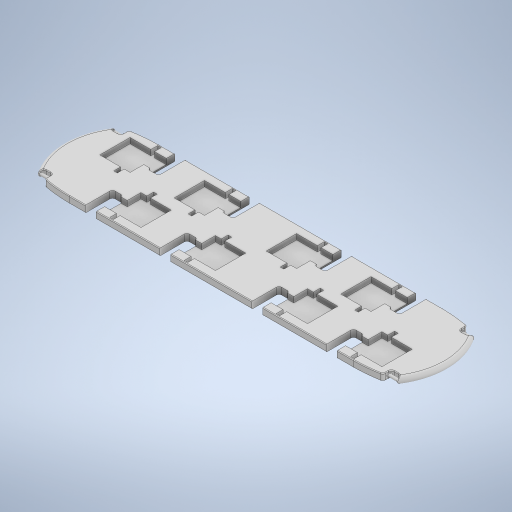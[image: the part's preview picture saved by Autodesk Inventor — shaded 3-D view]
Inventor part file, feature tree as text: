
AUTODESK INVENTOR PART (.ipt)
format: ipt  version: 2023.1 (Build 271208000, 208)  size: 1,013,760 bytes
history: native  units: mm
features: extrude x22, sketch x13, fillet x6
ambient origin geometry x8: Origin, YZ Plane, XZ Plane, XY Plane, X Axis, Y Axis, Z Axis, Center Point
bodies: Solid1 (feature_tree)
feature tree (41):
  sketch  "Sketch1"  dims[d0=250.0mm d1=66.0mm]
  extrude  "Extrusion1"  Depth=66.0mm
  sketch  "Sketch2"  dims[d3=34.0mm d4=55.0mm]
  extrude  "Extrusion2"  Depth=55.0mm
  extrude  "Extrusion3"  Depth=55.0mm
  extrude  "Extrusion20"  Depth=34.0mm
  fillet  "Fillet1"  Radius=55.0mm
  fillet  "Fillet2"  Radius=34.0mm
  fillet  "Fillet3"  Radius=55.0mm
  fillet  "Fillet4"  Radius=8.0mm
  extrude  "Extrusion21"  Depth=26.85mm
  extrude  "Extrusion22"  Depth=8.85mm
  extrude  "Extrusion23"  Depth=5.05mm
  extrude  "Extrusion24"  Depth=12.25mm
  fillet  "Fillet5"  Radius=2.65mm
  fillet  "Fillet6"  Radius=4.35mm
  sketch  "Sketch12"  dims[d26=5.0mm d27=0.0mm d28=4.0mm d29=0.0mm]
  sketch  "Sketch13"  dims[d53=2.65mm d54=4.35mm d55=4.35mm d56=2.65mm d57=12.25mm d58=4.45mm d59=5.05mm d60=5.05mm d61=8.85mm d62=26.85mm d63=32.45mm d64=8.0mm d65=20.0mm d66=55.0mm d67=34.0mm d68=55.0mm d69=34.0mm d71=0.0mm d72=5.0mm d74=0.0mm d75=4.0mm]
  sketch  "Sketch14"  dims[d76=1.15mm]
  sketch  "Sketch15"  dims[d78=2.65mm d79=4.35mm d80=4.35mm d81=2.65mm d82=12.25mm d83=4.45mm d84=5.05mm d85=5.05mm d86=8.85mm d87=26.85mm d88=32.45mm d89=8.0mm d90=20.0mm d91=55.0mm d92=34.0mm d93=55.0mm d94=34.0mm d96=0.0mm d97=5.0mm d99=0.0mm d100=4.0mm d101=1.15mm d103=2.65mm d104=4.35mm d105=4.35mm d106=2.65mm d107=12.25mm d108=4.45mm d109=5.05mm d110=5.05mm d111=8.85mm d112=26.85mm d113=32.45mm d114=8.0mm d115=20.0mm d116=55.0mm d117=34.0mm d118=55.0mm d119=34.0mm d121=0.0mm d122=5.0mm d124=0.0mm d125=4.0mm d126=1.15mm d127=2.65mm d128=4.35mm d129=4.35mm d130=2.65mm d131=12.25mm d133=5.05mm d135=8.85mm d136=26.85mm d137=32.45mm d138=8.0mm d139=20.0mm d140=55.0mm d141=34.0mm d142=55.0mm d145=0.0mm d146=5.0mm d148=0.0mm d149=4.0mm d150=1.15mm d151=22.35mm d152=5.05mm d154=4.45mm d156=2.65mm d157=4.35mm d158=4.35mm d159=2.65mm d160=5.05mm d161=4.45mm d162=22.35mm d163=12.25mm d164=5.05mm d165=8.85mm d166=26.85mm d167=32.45mm d168=8.0mm d169=20.0mm d170=55.0mm d171=34.0mm d172=55.0mm d174=0.0mm d175=5.0mm d177=0.0mm d178=4.0mm d180=1.15mm d182=2.65mm d183=4.35mm d184=4.35mm d185=2.65mm d186=5.05mm d187=4.45mm d188=22.35mm d189=12.25mm d190=5.05mm d191=8.85mm d192=26.85mm d193=32.45mm d194=8.0mm d195=20.0mm d196=55.0mm d197=34.0mm d198=55.0mm d200=0.0mm d201=5.0mm d203=0.0mm d204=4.0mm d205=34.0mm d207=2.65mm d208=4.35mm d209=4.35mm d210=2.65mm d211=5.05mm d212=4.45mm d213=22.35mm d214=12.25mm d215=5.05mm d216=8.85mm d217=26.85mm d218=32.45mm d219=8.0mm d220=20.0mm d221=55.0mm d222=34.0mm d223=55.0mm d224=34.0mm d226=0.0mm d227=5.0mm d229=0.0mm d230=4.0mm d231=7.0mm d232=7.0mm d233=50.0mm d234=50.0mm d235=13.0mm d236=66.0mm d237=13.0mm d238=66.0mm d239=20.0mm d240=25.0mm d241=40.0mm d242=5.0mm d243=0.0mm d244=50.0mm d245=2.5mm d246=2.0mm d247=0.5mm d248=2.0mm d249=7.5mm d250=0.0mm d251=7.5mm d252=0.0mm d253=2.0mm d254=7.5mm d255=0.0mm d256=2.0mm d257=7.5mm d258=0.0mm d259=0.4mm d260=0.4mm]
  sketch  "Sketch4"  dims[d5=34.0mm d6=55.0mm]
  sketch  "Sketch5"  dims[d7=5.0mm d8=0.0mm d9=34.0mm d10=55.0mm d11=34.0mm d12=55.0mm d13=8.0mm]
  sketch  "Sketch6"  dims[d14=20.0mm d15=26.85mm]
  sketch  "Sketch7"  dims[d16=32.45mm d17=8.85mm]
  sketch  "Sketch8"  dims[d18=5.05mm d19=5.05mm]
  sketch  "Sketch9"  dims[d20=4.45mm d21=12.25mm d22=2.65mm d23=4.35mm]
  sketch  "Sketch10"  dims[d24=4.35mm d25=2.65mm]
  extrude  "Extrusion6"  Depth=2.65mm
  extrude  "Extrusion7"  Depth=4.0mm TaperAngle=0.0deg
  extrude  "Extrusion8"  Depth=4.0mm TaperAngle=0.0deg
  extrude  "Extrusion9"  Depth=4.0mm TaperAngle=0.0deg
  extrude  "Extrusion10"  Depth=1.15mm
  extrude  "Extrusion11"  Depth=4.0mm TaperAngle=0.0deg
  extrude  "Extrusion12"  Depth=1.15mm
  extrude  "Extrusion13"  Depth=4.0mm TaperAngle=0.0deg
  extrude  "Extrusion14"  Depth=1.15mm
  extrude  "Extrusion15"  Depth=22.35mm
  extrude  "Extrusion16"  Depth=5.05mm
  extrude  "Extrusion17"  Depth=4.45mm
  extrude  "Extrusion18"  Depth=4.0mm TaperAngle=0.0deg
  extrude  "Extrusion19"  Depth=1.15mm
